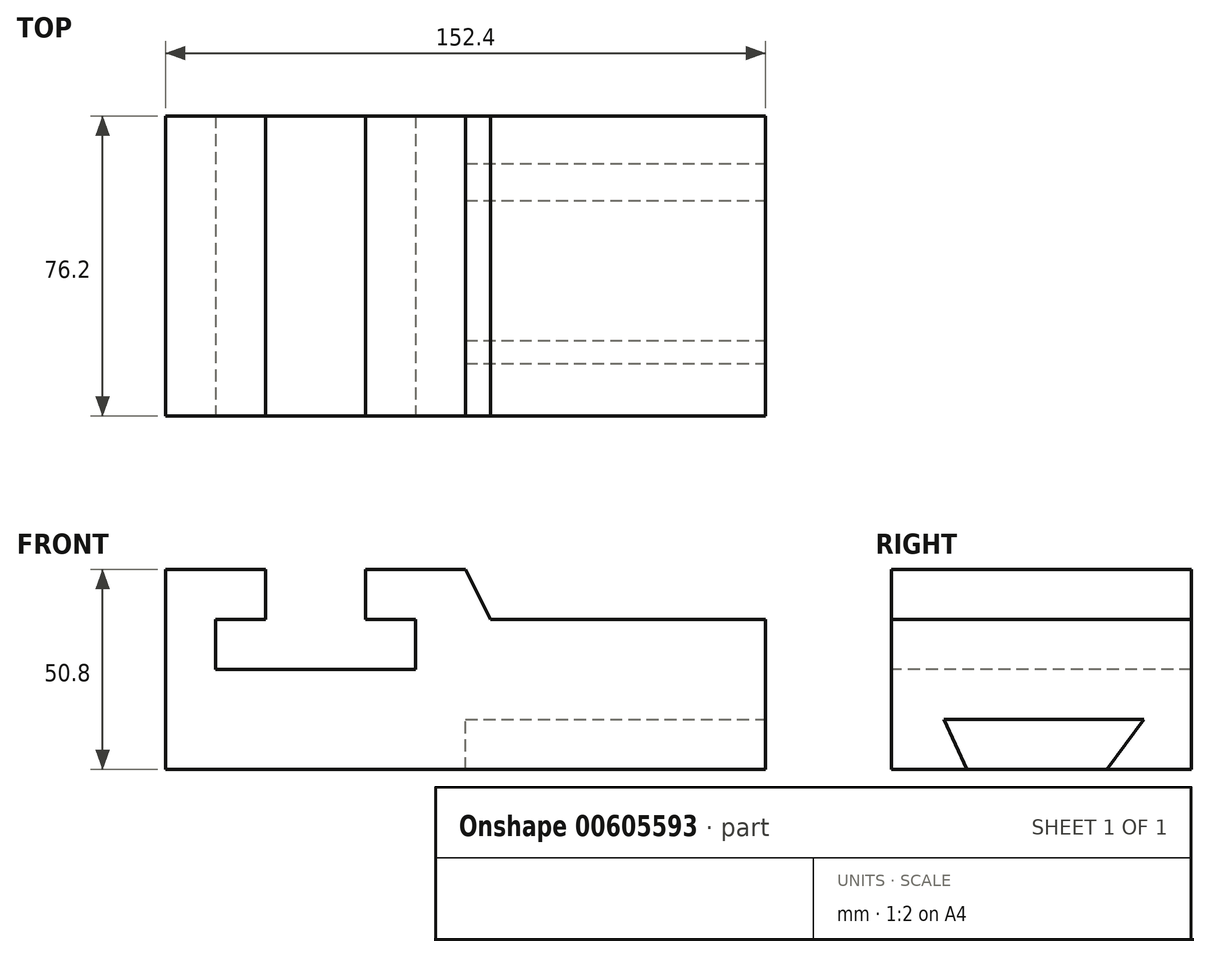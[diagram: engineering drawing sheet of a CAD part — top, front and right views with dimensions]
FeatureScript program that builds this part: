
annotation { "Feature Type Name" : "Feature", "Feature Type Description" : "" }
export const myFeature = defineFeature(function(context is Context, id is Id, definition is map)
    precondition{}
    {
        {
            var Q0;
            Q0=qCreatedBy(makeId("Front.planeOp"),FACE);
            var sketch = newSketch(context, id + "F0", { "sketchPlane" : qUnion([Q0])});
            skLineSegment(sketch, "E0", {"start": v(0, 0) * mm, "end": v(0, 50.8) * mm});
            skLineSegment(sketch, "E1", {"start": v(0, 50.8) * mm, "end": v(25.4, 50.8) * mm});
            skLineSegment(sketch, "E2", {"start": v(25.4, 50.8) * mm, "end": v(25.4, 38.1) * mm});
            skLineSegment(sketch, "E3", {"start": v(25.4, 38.1) * mm, "end": v(12.7, 38.1) * mm});
            skLineSegment(sketch, "E4", {"start": v(12.7, 38.1) * mm, "end": v(12.7, 25.4) * mm});
            skLineSegment(sketch, "E5", {"start": v(12.7, 25.4) * mm, "end": v(63.5, 25.4) * mm});
            skLineSegment(sketch, "E6", {"start": v(63.5, 25.4) * mm, "end": v(63.5, 38.1) * mm});
            skLineSegment(sketch, "E7", {"start": v(63.5, 38.1) * mm, "end": v(50.8, 38.1) * mm});
            skLineSegment(sketch, "E8", {"start": v(50.8, 38.1) * mm, "end": v(50.8, 50.8) * mm});
            skLineSegment(sketch, "E9", {"start": v(50.8, 50.8) * mm, "end": v(76.2, 50.8) * mm});
            skLineSegment(sketch, "E10", {"start": v(76.2, 50.8) * mm, "end": v(82.55, 38.1) * mm});
            skLineSegment(sketch, "E11", {"start": v(82.55, 38.1) * mm, "end": v(152.4, 38.1) * mm});
            skLineSegment(sketch, "E12", {"start": v(152.4, 38.1) * mm, "end": v(152.4, 0) * mm});
            skLineSegment(sketch, "E13", {"start": v(152.4, 0) * mm, "end": v(0, 0) * mm});
            skSolve(sketch);
        }
        {
            var Q0;
            Q0=makeQuery(id+"F0.imprint","IMPRINT",FACE,{"disambiguationData":[TD([[makeQuery(id+"F0.imprint","IMPRINT",EDGE,{"derivedFrom":sQuery(id+"F0.wireOp",EDGE,"E0")}),-1.0]])]});
            extrude(context, id + "F1", {"entities" : qUnion([Q0]), "oppositeDirection" : true, "depth" : 76.2 * mm, "offsetDistance" : 25.4 * mm});
        }
        {
            var Q0;
            Q0=makeQuery(id+"F1.opExtrude","SWEPT_FACE",FACE,{"disambiguationData":[OSD([sQuery(id+"F0.wireOp",EDGE,"E12")])]});
            var sketch = newSketch(context, id + "F2", { "sketchPlane" : qUnion([Q0])});
            skLineSegment(sketch, "E14", {"start": v(19.16, 0) * mm, "end": v(13.4, 12.7) * mm});
            skLineSegment(sketch, "E15", {"start": v(13.4, 12.7) * mm, "end": v(64.2, 12.7) * mm});
            skLineSegment(sketch, "E16", {"start": v(64.2, 12.7) * mm, "end": v(54.77, 0) * mm});
            skSolve(sketch);
        }
        {
            var Q0;
            {var subQ0=sQuery(id+"F2.wireOp",EDGE,"E14");Q0=makeQuery(id+"F2.imprint","IMPRINT",FACE,{"disambiguationData":[TD([[makeQuery(id+"F2.imprint","IMPRINT",EDGE,{"derivedFrom":subQ0}),-1.0]])]});}
            extrude(context, id + "F3", {"entities" : qUnion([Q0]), "operationType" : NewBodyOperationType.REMOVE, "oppositeDirection" : true, "depth" : 76.2 * mm, "offsetDistance" : 25.4 * mm});
        }
    });
